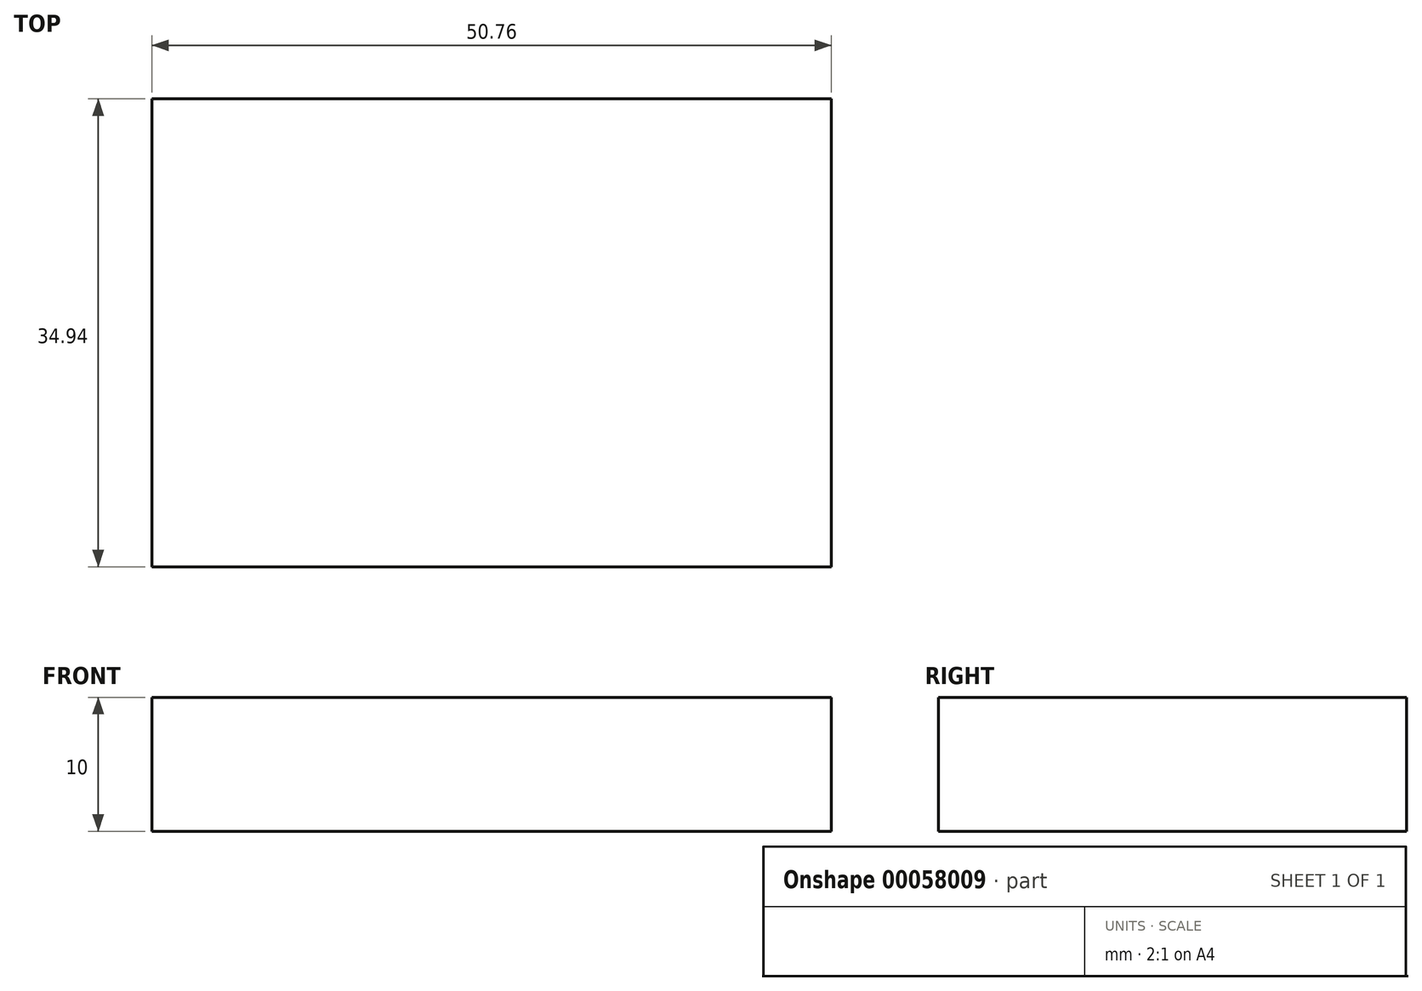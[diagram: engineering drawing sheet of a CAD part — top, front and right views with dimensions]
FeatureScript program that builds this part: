
annotation { "Feature Type Name" : "Feature", "Feature Type Description" : "" }
export const myFeature = defineFeature(function(context is Context, id is Id, definition is map)
    precondition{}
    {
        {
            var Q0;
            Q0=qCreatedBy(makeId("Top.planeOp"),FACE);
            var sketch = newSketch(context, id + "F0", { "sketchPlane" : qUnion([Q0])});
            skLineSegment(sketch, "E0.bottom", {"start": v(-21.96, -17.11) * mm, "end": v(28.8, -17.11) * mm});
            skLineSegment(sketch, "E0.top", {"start": v(-21.96, 17.83) * mm, "end": v(28.8, 17.83) * mm});
            skLineSegment(sketch, "E0.left", {"start": v(-21.96, -17.11) * mm, "end": v(-21.96, 17.83) * mm});
            skLineSegment(sketch, "E0.right", {"start": v(28.8, -17.11) * mm, "end": v(28.8, 17.83) * mm});
            skSolve(sketch);
        }
        {
            var Q0;
            Q0=makeQuery(id+"F0.imprint","IMPRINT",FACE,{"disambiguationData":[TD([[makeQuery(id+"F0.imprint","IMPRINT",EDGE,{"derivedFrom":sQuery(id+"F0.wireOp",EDGE,"E0.bottom")}),1.0]])]});
            extrude(context, id + "F1", {"entities" : qUnion([Q0]), "depth" : 10 * mm});
        }
    });
